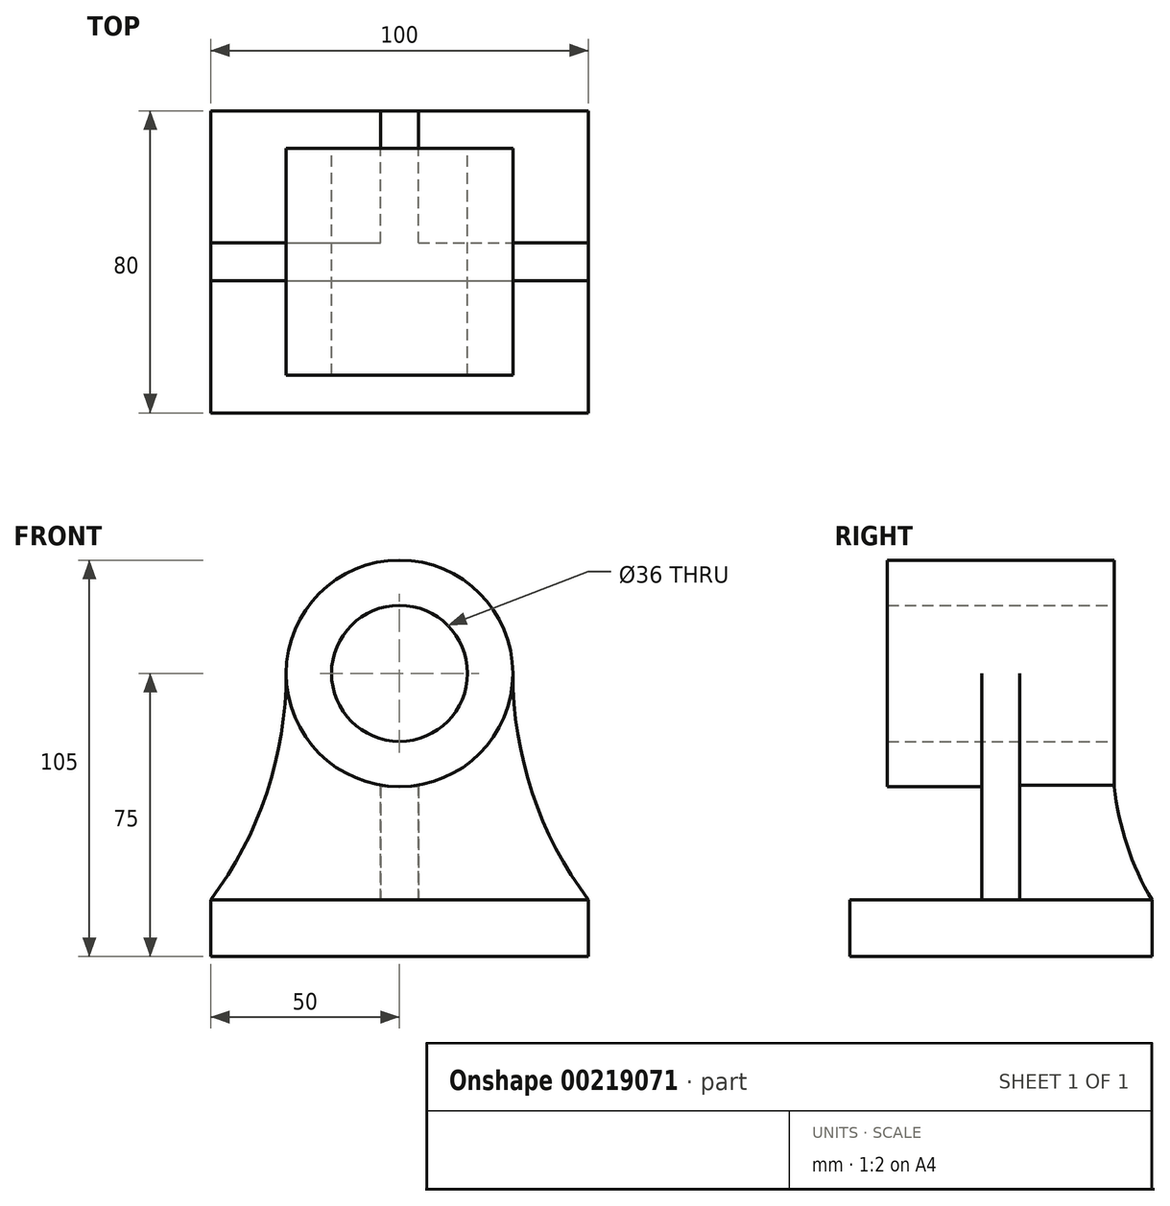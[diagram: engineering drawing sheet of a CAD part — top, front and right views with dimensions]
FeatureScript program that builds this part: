
annotation { "Feature Type Name" : "Feature", "Feature Type Description" : "" }
export const myFeature = defineFeature(function(context is Context, id is Id, definition is map)
    precondition{}
    {
        {
            var Q0;
            Q0=qCreatedBy(makeId("Front.planeOp"),FACE);
            var sketch = newSketch(context, id + "F0", { "sketchPlane" : qUnion([Q0])});
            skLineSegment(sketch, "E0.bottom", {"start": v(-50, 15) * mm, "end": v(50, 15) * mm});
            skLineSegment(sketch, "E0.top", {"start": v(-50, 0) * mm, "end": v(50, 0) * mm});
            skLineSegment(sketch, "E0.left", {"start": v(-50, 15) * mm, "end": v(-50, 0) * mm});
            skLineSegment(sketch, "E0.right", {"start": v(50, 15) * mm, "end": v(50, 0) * mm});
            skCircle(sketch, "E1", {"center": v(0, 75) * mm, "radius": 30 * mm});
            skCircle(sketch, "E2", {"center": v(0, 75) * mm, "radius": 18 * mm});
            skArc(sketch, "E3", {"start": v(-50, 15) * mm, "mid": v(-35.13, 43.38) * mm, "end": v(-30, 75) * mm});
            skArc(sketch, "E4.MirrorC", {"start": v(50, 15) * mm, "mid": v(35.13, 43.38) * mm, "end": v(30, 75) * mm});
            skSolve(sketch);
        }
        {
            var Q0;
            Q0=makeQuery(id+"F0.imprint","IMPRINT",FACE,{"disambiguationData":[TD([[makeQuery(id+"F0.imprint","IMPRINT",EDGE,{"derivedFrom":sQuery(id+"F0.wireOp",EDGE,"E0.bottom")}),-1.0]])]});
            extrude(context, id + "F1", {"entities" : qUnion([Q0]), "endBound" : BoundingType.SYMMETRIC, "depth" : 80 * mm});
        }
        {
            var Q0;
            Q0=makeQuery(id+"F0.imprint","IMPRINT",FACE,{"disambiguationData":[TD([[makeQuery(id+"F0.imprint","IMPRINT",EDGE,{"derivedFrom":sQuery(id+"F0.wireOp",EDGE,"E0.bottom")}),1.0]])]});
            extrude(context, id + "F2", {"entities" : qUnion([Q0]), "operationType" : NewBodyOperationType.ADD, "endBound" : BoundingType.SYMMETRIC, "depth" : 10 * mm});
        }
        {
            var Q0;
            Q0=makeQuery(id+"F0.imprint","IMPRINT",FACE,{"disambiguationData":[TD([[makeQuery(id+"F0.imprint","IMPRINT",EDGE,{"derivedFrom":sQuery(id+"F0.wireOp",EDGE,"E2")}),-1.0]])]});
            extrude(context, id + "F3", {"entities" : qUnion([Q0]), "operationType" : NewBodyOperationType.ADD, "endBound" : BoundingType.SYMMETRIC, "depth" : 60 * mm});
        }
        {
            var Q0;
            Q0=qCreatedBy(makeId("Right.planeOp"),FACE);
            var sketch = newSketch(context, id + "F4", { "sketchPlane" : qUnion([Q0])});
            skArc(sketch, "E5", {"start": v(30, 45) * mm, "mid": v(33.4, 29.47) * mm, "end": v(40, 15) * mm});
            skPoint(sketch, "E6.end.orphan", {"position": v(5, 15) * mm});
            skPoint(sketch, "E6.start.orphan", {"position": v(40, 15) * mm});
            skPoint(sketch, "E7.orphan", {"position": v(30, 105) * mm});
            skPoint(sketch, "E8.start.orphan", {"position": v(-30, 105) * mm});
            skLineSegment(sketch, "E9.0", {"start": v(5, 15) * mm, "end": v(5, 50) * mm});
            skLineSegment(sketch, "E10.0", {"start": v(5, 15) * mm, "end": v(40, 15) * mm});
            skPoint(sketch, "E11.orphan", {"position": v(5, 75) * mm});
            skLineSegment(sketch, "E12", {"start": v(5, 50) * mm, "end": v(30, 50) * mm});
            skLineSegment(sketch, "E13", {"start": v(30, 50) * mm, "end": v(30, 45) * mm});
            skSolve(sketch);
        }
        {
            var Q0;
            Q0=makeQuery(id+"F4.imprint","IMPRINT",FACE,{"disambiguationData":[TD([[makeQuery(id+"F4.imprint","IMPRINT",EDGE,{"derivedFrom":sQuery(id+"F4.wireOp",EDGE,"E5")}),-1.0]])]});
            extrude(context, id + "F5", {"entities" : qUnion([Q0]), "operationType" : NewBodyOperationType.ADD, "endBound" : BoundingType.SYMMETRIC, "depth" : 10 * mm});
        }
    });
